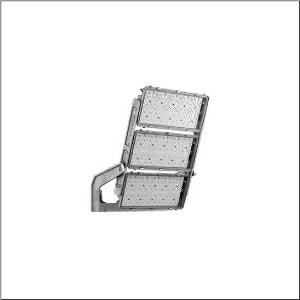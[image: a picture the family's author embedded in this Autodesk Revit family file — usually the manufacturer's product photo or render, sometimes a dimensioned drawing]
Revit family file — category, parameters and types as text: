
# Revit family: floodlight_fl_11_maxi_pro_remote___pl52_5xa779427d01aa_0793
name_source: partatom
category: Lighting Fixtures
units: mm (PartAtom-declared; Revit-internal decimal feet)

## family parameters
Cut with Voids When Loaded = No
Host = Face
Light Source = No
Part Type = Normal
Room Calculation Point = No
Round Connector Dimension = Use Diameter
Shared = No

## types (1)
- --- (1 x LED, 173640 lm, 1425.5 W, 5000K)
    Apparent Load = 1425 VA
    CIE Flux Codes = 24 55 98 100 100
    Color Rendering = 70
    Color Temperature = 5000K
    Default Elevation = 1800 mm
    Description = Floodlight FL 11  maxi  pro Remote floodlight; light control with lens of PMMA; cover panel of toughened safety glass, transparent; light distribution: PL52, asymmetric direct distribution, LEDcolour temperature: 5000K, rated luminous flux: 173.640lm, colour rendering: CRI > 70, light colour: 750; luminous efficacy: 122lm/W; brightness control: DALI 2 (1 DALI address); with terminal, 8-pole, max. 2.5mm², mains connection: 220..240V/380..400V AC, 50/60Hz, surge voltage resistance: line to ground: 10kV, ECG replaceable separately, LED unit replaceable without ESD environment, dustproof LED module, dimming range 10..100%, no afterglow with DALI off / DMX off command; 1426W floodlight with 3x LED unit of diecast aluminium, coated grey; length: 713mm / width: 651mm / height: 338mm; mounting bracket, of diecast aluminium, uncoated, natural, equipment: Power, protection rating (complete): IP66; insulation class (complete): insulation class I (protective earthing); certification: CE, ENEC, VDE; ball protection: ball impact resistance with accessories, rated ambient temperature 10°C, only for outdoor installations, permissible operating ambient temperature: -40..+30°C, permissible storage temperature: -40..+85°C; packaging unit: 1 piece

Light Distribution: PL52
    Height = 320 mm
    Lamp = 1 x LED
    Lamp Light Flux = 173640 lm
    Lamp Power = 1425.5 W
    Lamp count = 1
    Length = 1002 mm
    Luminous efficacy = 122 lm/W
    Manufacturer = Siteco
    ModVariant = No
    Model = 5XA779427D01AA
    Number of Poles = 1
    OnlyDefault = Yes
    Power Factor = 1
    Product Name = Floodlight FL 11 maxi pro Remote | PL52
    Product group = floodlight | pylon top
    ProductGroupID = 6101
    Protection Class = Protection class I
    Protection Degree = IP 66
    RLX_Detail_Level = 1
    RlxData = <blob elided: 52409 chars, md5=64bb104e>
    Socket = socket
    Standby Power = 0 W
    System Light Flux = 173640 lm
    System Power = 1425 W
    Type Comments = factory setting: luminous flux: 100 % | dim-lin: 254 | 980 mA
    Type Image = l_1006784.jpg
    URL = http://relux.com
    VarID = @adj_007547
    Voltage = 0 V
    Weight = 0.00 kg
    Width = 655 mm

## geometry (parser evidence)
native form markers: Blend x4, Sweep x14
no freeform markers — native parametric forms only
